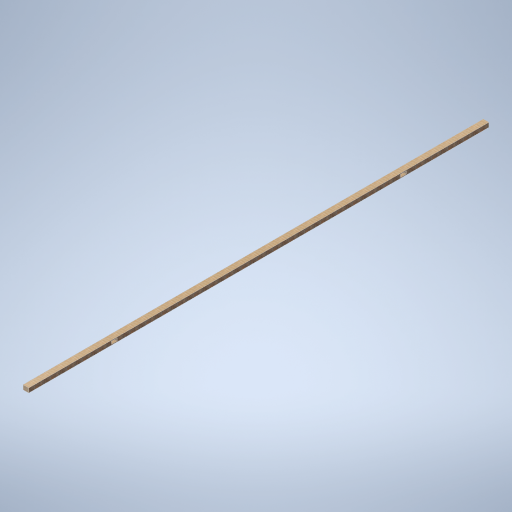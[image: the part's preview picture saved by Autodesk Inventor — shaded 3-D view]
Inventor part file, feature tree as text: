
AUTODESK INVENTOR PART (.ipt)
format: ipt  version: 2024.2 (Build 282272000, 272)  size: 276,992 bytes
history: native  units: mm
features: extrude x2, sketch x2
ambient origin geometry x8: Origin, YZ Plane, XZ Plane, XY Plane, X Axis, Y Axis, Z Axis, Center Point
bodies: Solid1 (feature_tree)
feature tree (4):
  extrude  "Extrusion1"  Depth=400.0mm
  extrude  "Extrusion2"  Depth=200.0mm TaperAngle=0.0deg
  sketch  "Sketch1"  dims[d0=32302.0mm d1=0.0mm d3=400.0mm]
  sketch  "Sketch2"  dims[d4=200.0mm d5=200.0mm d6=0.0mm]
